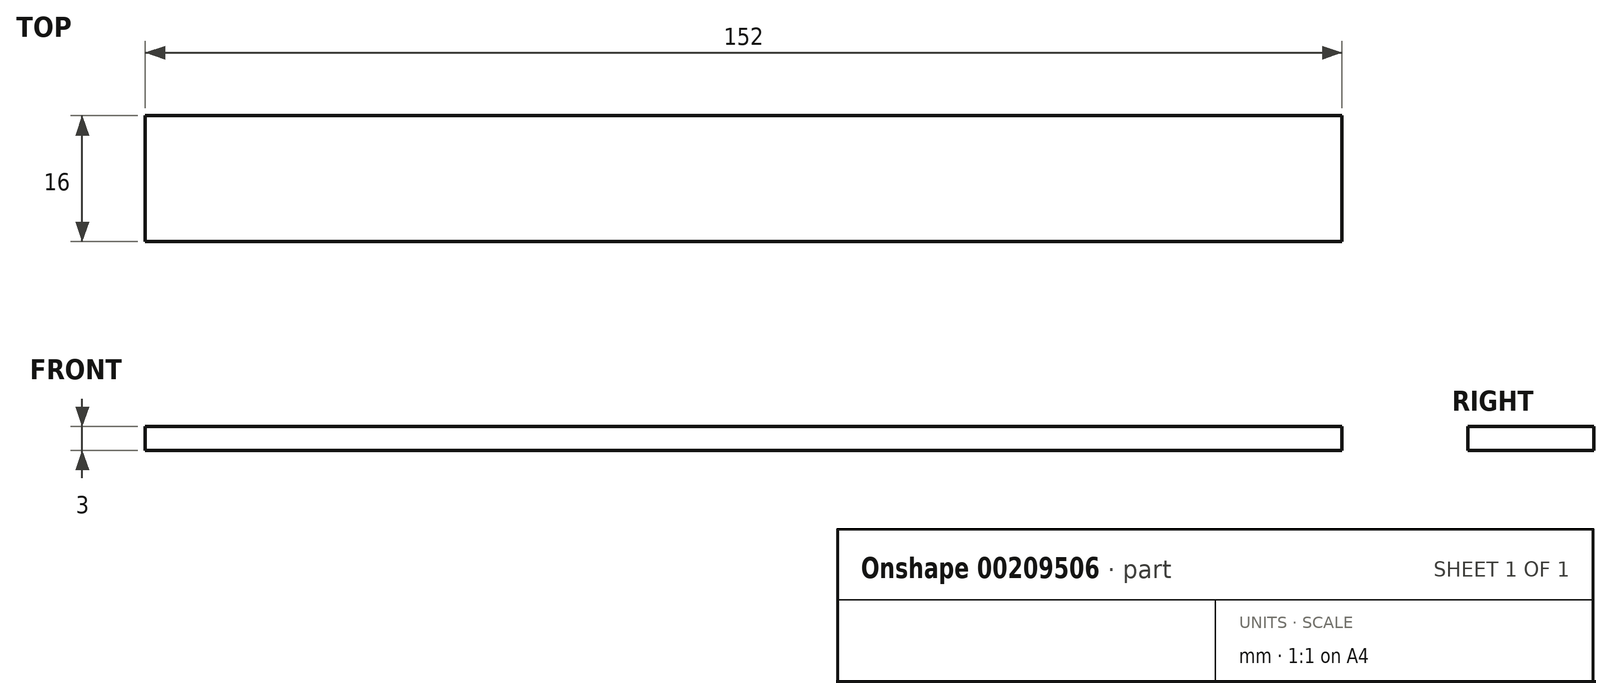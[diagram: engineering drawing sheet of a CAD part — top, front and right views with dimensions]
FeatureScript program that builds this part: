
annotation { "Feature Type Name" : "Feature", "Feature Type Description" : "" }
export const myFeature = defineFeature(function(context is Context, id is Id, definition is map)
    precondition{}
    {
        {
            var Q0;
            Q0=qCreatedBy(makeId("Top.planeOp"),FACE);
            var sketch = newSketch(context, id + "F0", { "sketchPlane" : qUnion([Q0])});
            skLineSegment(sketch, "E0.bottom", {"start": v(-76, 8) * mm, "end": v(76, 8) * mm});
            skLineSegment(sketch, "E0.top", {"start": v(-76, -8) * mm, "end": v(76, -8) * mm});
            skLineSegment(sketch, "E0.left", {"start": v(-76, 8) * mm, "end": v(-76, -8) * mm});
            skLineSegment(sketch, "E0.right", {"start": v(76, 8) * mm, "end": v(76, -8) * mm});
            skPoint(sketch, "E0.middle", {"position": v(0, 0) * mm});
            skSolve(sketch);
        }
        {
            var Q0;
            Q0 = qSketchRegion(id + "F0", true);
            extrude(context, id + "F1", {"entities" : qUnion([Q0]), "depth" : 3 * mm});
        }
    });
